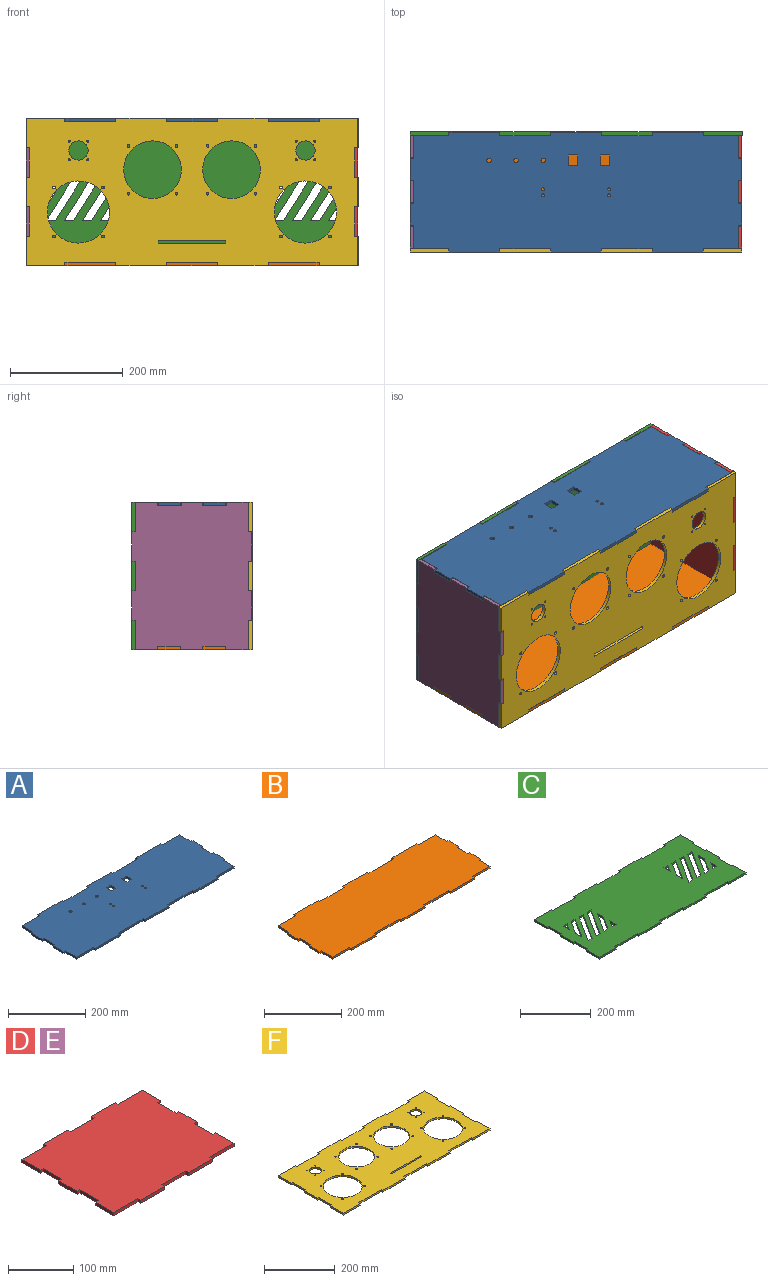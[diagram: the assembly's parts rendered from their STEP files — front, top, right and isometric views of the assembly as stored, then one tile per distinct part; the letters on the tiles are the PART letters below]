
ASSEMBLY  parts=6 mates=5
PART A: 61 faces, bbox 588x212x6 mm
  f0: plane 40x6mm, normal (-1,0,0), area 240mm2, adj f1,f58,f59,f60
  f1: plane 63x6mm, normal (0,-1,0), area 378mm2, adj f0,f2,f59,f60
  f2: plane 6x6mm, normal (-1,0,0), area 36mm2, adj f1,f3,f59,f60
  f3: plane 90x6mm, normal (0,-1,0), area 540mm2, adj f2,f4,f59,f60
  f4: plane 6x6mm, normal (1,0,0), area 36mm2, adj f3,f5,f59,f60
  f5: plane 90x6mm, normal (0,-1,0), area 540mm2, adj f4,f6,f59,f60
  f6: plane 6x6mm, normal (-1,0,0), area 36mm2, adj f5,f7,f59,f60
  f7: plane 90x6mm, normal (0,-1,0), area 540mm2, adj f6,f8,f59,f60
  f8: plane 6x6mm, normal (1,0,0), area 36mm2, adj f7,f9,f59,f60
  f9: plane 90x6mm, normal (0,-1,0), area 540mm2, adj f8,f10,f59,f60
  f10: plane 6x6mm, normal (-1,0,0), area 36mm2, adj f9,f11,f59,f60
  f11: plane 90x6mm, normal (0,-1,0), area 540mm2, adj f10,f12,f59,f60
  f12: plane 6x6mm, normal (1,0,0), area 36mm2, adj f11,f13,f59,f60
  f13: plane 63x6mm, normal (0,-1,0), area 378mm2, adj f12,f14,f59,f60
  f14: plane 40x6mm, normal (1,0,0), area 240mm2, adj f13,f15,f59,f60
  f15: plane 6x6mm, normal (0,-1,0), area 36mm2, adj f14,f16,f59,f60
  f16: plane 40x6mm, normal (1,0,0), area 240mm2, adj f15,f17,f59,f60
  f17: plane 6x6mm, normal (0,1,0), area 36mm2, adj f16,f18,f59,f60
  f18: plane 40x6mm, normal (1,0,0), area 240mm2, adj f17,f19,f59,f60
  f19: plane 6x6mm, normal (0,-1,0), area 36mm2, adj f18,f20,f59,f60
  f20: plane 40x6mm, normal (1,0,0), area 240mm2, adj f19,f21,f59,f60
  f21: plane 6x6mm, normal (0,1,0), area 36mm2, adj f20,f22,f59,f60
  f22: plane 40x6mm, normal (1,0,0), area 240mm2, adj f21,f23,f59,f60
  f23: plane 63x6mm, normal (0,1,0), area 378mm2, adj f22,f24,f59,f60
  f24: plane 6x6mm, normal (1,0,0), area 36mm2, adj f23,f25,f59,f60
  f25: plane 90x6mm, normal (0,1,0), area 540mm2, adj f24,f26,f59,f60
  f26: plane 6x6mm, normal (-1,0,0), area 36mm2, adj f25,f27,f59,f60
  f27: plane 90x6mm, normal (0,1,0), area 540mm2, adj f26,f28,f59,f60
  f28: plane 6x6mm, normal (1,0,0), area 36mm2, adj f27,f29,f59,f60
  f29: plane 90x6mm, normal (0,1,0), area 540mm2, adj f28,f30,f59,f60
  f30: plane 6x6mm, normal (-1,0,0), area 36mm2, adj f29,f31,f59,f60
  f31: plane 90x6mm, normal (0,1,0), area 540mm2, adj f30,f32,f59,f60
  f32: plane 6x6mm, normal (1,0,0), area 36mm2, adj f31,f33,f59,f60
  f33: plane 90x6mm, normal (0,1,0), area 540mm2, adj f32,f34,f59,f60
  f34: plane 6x6mm, normal (-1,0,0), area 36mm2, adj f33,f35,f59,f60
  f35: plane 63x6mm, normal (0,1,0), area 378mm2, adj f34,f36,f59,f60
  f36: plane 40x6mm, normal (-1,0,0), area 240mm2, adj f35,f37,f59,f60
  f37: plane 6x6mm, normal (0,1,0), area 36mm2, adj f36,f38,f59,f60
  f38: plane 40x6mm, normal (-1,0,0), area 240mm2, adj f37,f39,f59,f60
  f39: plane 6x6mm, normal (0,-1,0), area 36mm2, adj f38,f40,f59,f60
  f40: plane 40x6mm, normal (-1,0,0), area 240mm2, adj f39,f41,f59,f60
  f41: plane 6x6mm, normal (0,1,0), area 36mm2, adj f40,f42,f59,f60
  f42: plane 40x6mm, normal (-1,0,0), area 240mm2, adj f41,f58,f59,f60
  f43: plane 19x6mm, normal (1,0,0), area 114mm2, adj f44,f56,f59,f60
  f44: plane 17x6mm, normal (0,-1,0), area 102mm2, adj f43,f45,f59,f60
  f45: plane 19x6mm, normal (-1,0,0), area 114mm2, adj f44,f56,f59,f60
  f46: plane 19x6mm, normal (1,0,0), area 114mm2, adj f47,f57,f59,f60
  f47: plane 17x6mm, normal (0,-1,0), area 102mm2, adj f46,f48,f59,f60
  f48: plane 19x6mm, normal (-1,0,0), area 114mm2, adj f47,f57,f59,f60
  f49: cylinder r=4mm len=8mm, axis (0,0,-1), area 150.8mm2, adj f59,f60
  f50: cylinder r=4mm len=8mm, axis (0,0,-1), area 150.8mm2, adj f59,f60
  f51: cylinder r=4mm len=8mm, axis (0,0,-1), area 150.8mm2, adj f59,f60
  f52: cylinder r=2.5mm len=6mm, axis (0,0,-1), area 94.2mm2, adj f59,f60
  f53: cylinder r=2.5mm len=6mm, axis (0,0,-1), area 94.2mm2, adj f59,f60
  f54: cylinder r=2.5mm len=6mm, axis (0,0,-1), area 94.2mm2, adj f59,f60
  f55: cylinder r=2.5mm len=6mm, axis (0,0,-1), area 94.2mm2, adj f59,f60
  f56: plane 17x6mm, normal (0,1,0), area 102mm2, adj f43,f45,f59,f60
  f57: plane 17x6mm, normal (0,1,0), area 102mm2, adj f46,f48,f59,f60
  f58: plane 6x6mm, normal (0,-1,0), area 36mm2, adj f0,f42,f59,f60
  f59: plane 588x212mm, normal (0,0,1), area 118524.7mm2, adj f0,f1,f2,f3,f4,f5,f6,f7
  f60: plane 588x212mm, normal (0,0,-1), area 118524.7mm2, adj f0,f1,f2,f3,f4,f5,f6,f7
PART B: 46 faces, bbox 588x213.1x6 mm
  f0: plane 40x6mm, normal (-1,0,0), area 240mm2, adj f1,f43,f44,f45
  f1: plane 6x6mm, normal (0,-1,0), area 36mm2, adj f0,f2,f44,f45
  f2: plane 40x6mm, normal (-1,0,0), area 240mm2, adj f1,f3,f44,f45
  f3: plane 6x6mm, normal (0,1,0), area 36mm2, adj f2,f4,f44,f45
  f4: plane 40x6mm, normal (-1,0,0), area 240mm2, adj f3,f5,f44,f45
  f5: plane 6x6mm, normal (0,-1,0), area 36mm2, adj f4,f6,f44,f45
  f6: plane 40x6mm, normal (-1,0,0), area 240mm2, adj f5,f7,f44,f45
  f7: plane 63x6mm, normal (0,-1,0), area 378mm2, adj f6,f8,f44,f45
  f8: plane 6.78x6mm, normal (-1,0,0), area 40.7mm2, adj f7,f9,f44,f45
  f9: plane 90x6mm, normal (0,-1,0), area 540mm2, adj f8,f10,f44,f45
  f10: plane 6x6mm, normal (1,0,0), area 36mm2, adj f9,f11,f44,f45
  f11: plane 90x6mm, normal (0,-1,0), area 540mm2, adj f10,f12,f44,f45
  f12: plane 6x6mm, normal (-1,0,0), area 36mm2, adj f11,f13,f44,f45
  f13: plane 90x6mm, normal (0,-1,0), area 540mm2, adj f12,f14,f44,f45
  f14: plane 6x6mm, normal (1,0,0), area 36mm2, adj f13,f15,f44,f45
  f15: plane 90x6mm, normal (0,-1,0), area 540mm2, adj f14,f16,f44,f45
  f16: plane 6.4x6mm, normal (-1,0,0), area 38.4mm2, adj f15,f17,f44,f45
  f17: plane 90x6mm, normal (0,-1,0), area 540mm2, adj f16,f18,f44,f45
  f18: plane 7.14x6mm, normal (1,0,0), area 42.8mm2, adj f17,f19,f44,f45
  f19: plane 63x6mm, normal (0,-1,0), area 378mm2, adj f18,f20,f44,f45
  f20: plane 40x6mm, normal (1,0,0), area 240mm2, adj f19,f21,f44,f45
  f21: plane 6x6mm, normal (0,-1,0), area 36mm2, adj f20,f22,f44,f45
  f22: plane 40x6mm, normal (1,0,0), area 240mm2, adj f21,f23,f44,f45
  f23: plane 6x6mm, normal (0,1,0), area 36mm2, adj f22,f24,f44,f45
  f24: plane 40x6mm, normal (1,0,0), area 240mm2, adj f23,f25,f44,f45
  f25: plane 6x6mm, normal (0,-1,0), area 36mm2, adj f24,f26,f44,f45
  f26: plane 40x6mm, normal (1,0,0), area 240mm2, adj f25,f27,f44,f45
  f27: plane 6x6mm, normal (0,1,0), area 36mm2, adj f26,f28,f44,f45
  f28: plane 40x6mm, normal (1,0,0), area 240mm2, adj f27,f29,f44,f45
  f29: plane 63x6mm, normal (0,1,0), area 378mm2, adj f28,f30,f44,f45
  f30: plane 6x6mm, normal (1,0,0), area 36mm2, adj f29,f31,f44,f45
  f31: plane 90x6mm, normal (0,1,0), area 540mm2, adj f30,f32,f44,f45
  f32: plane 6x6mm, normal (-1,0,0), area 36mm2, adj f31,f33,f44,f45
  f33: plane 90x6mm, normal (0,1,0), area 540mm2, adj f32,f34,f44,f45
  f34: plane 6x6mm, normal (1,0,0), area 36mm2, adj f33,f35,f44,f45
  f35: plane 90x6mm, normal (0,1,0), area 540mm2, adj f34,f36,f44,f45
  f36: plane 6x6mm, normal (-1,0,0), area 36mm2, adj f35,f37,f44,f45
  f37: plane 90x6mm, normal (0,1,0), area 540mm2, adj f36,f38,f44,f45
  f38: plane 6x6mm, normal (1,0,0), area 36mm2, adj f37,f39,f44,f45
  f39: plane 90x6mm, normal (0,1,0), area 540mm2, adj f38,f40,f44,f45
  f40: plane 6x6mm, normal (-1,0,0), area 36mm2, adj f39,f41,f44,f45
  f41: plane 63x6mm, normal (0,1,0), area 378mm2, adj f40,f42,f44,f45
  f42: plane 40x6mm, normal (-1,0,0), area 240mm2, adj f41,f43,f44,f45
  f43: plane 6x6mm, normal (0,1,0), area 36mm2, adj f0,f42,f44,f45
  f44: plane 588x213.14mm, normal (0,0,1), area 119768.4mm2, adj f0,f1,f2,f3,f4,f5,f6,f7
  f45: plane 588x213.14mm, normal (0,0,-1), area 119768.4mm2, adj f0,f1,f2,f3,f4,f5,f6,f7
PART C: 90 faces, bbox 588x261x6 mm
  f0: plane 25x6mm, normal (1,0,0), area 150mm2, adj f1,f87,f88,f89
  f1: plane 16x6mm, normal (0,-1,0), area 96mm2, adj f0,f87,f88,f89
  f2: plane 25x16mm, normal (0.84,-0.54,0), area 178.1mm2, adj f3,f75,f88,f89
  f3: plane 25x6mm, normal (-1,0,0), area 150mm2, adj f2,f75,f88,f89
  f4: plane 16x6mm, normal (0,1,0), area 96mm2, adj f5,f76,f88,f89
  f5: plane 25x16mm, normal (0.84,-0.54,0), area 178.1mm2, adj f4,f76,f88,f89
  f6: plane 75x48mm, normal (0.84,-0.54,0), area 534.3mm2, adj f7,f77,f88,f89
  f7: plane 25x6mm, normal (-1,0,0), area 150mm2, adj f6,f8,f88,f89
  f8: plane 50x32mm, normal (-0.84,0.54,0), area 356.2mm2, adj f7,f77,f88,f89
  f9: plane 100x64mm, normal (0.84,-0.54,0), area 712.4mm2, adj f10,f78,f88,f89
  f10: plane 16x6mm, normal (0,-1,0), area 96mm2, adj f9,f11,f88,f89
  f11: plane 100x64mm, normal (-0.84,0.54,0), area 712.4mm2, adj f10,f78,f88,f89
  f12: plane 100x64mm, normal (0.84,-0.54,0), area 712.4mm2, adj f13,f79,f88,f89
  f13: plane 16x6mm, normal (0,-1,0), area 96mm2, adj f12,f14,f88,f89
  f14: plane 100x64mm, normal (-0.84,0.54,0), area 712.4mm2, adj f13,f79,f88,f89
  f15: plane 50x32mm, normal (0.84,-0.54,0), area 356.2mm2, adj f16,f80,f88,f89
  f16: plane 16x6mm, normal (0,-1,0), area 96mm2, adj f15,f17,f88,f89
  f17: plane 75x48mm, normal (-0.84,0.54,0), area 534.3mm2, adj f16,f80,f88,f89
  f18: plane 16x6mm, normal (0,-1,0), area 96mm2, adj f19,f81,f88,f89
  f19: plane 25x16mm, normal (-0.84,0.54,0), area 178.1mm2, adj f18,f81,f88,f89
  f20: plane 75x48mm, normal (0.84,-0.54,0), area 534.3mm2, adj f21,f82,f88,f89
  f21: plane 25x6mm, normal (-1,0,0), area 150mm2, adj f20,f22,f88,f89
  f22: plane 50x32mm, normal (-0.84,0.54,0), area 356.2mm2, adj f21,f82,f88,f89
  f23: plane 100x64mm, normal (0.84,-0.54,0), area 712.4mm2, adj f24,f83,f88,f89
  f24: plane 16x6mm, normal (0,-1,0), area 96mm2, adj f23,f25,f88,f89
  f25: plane 100x64mm, normal (-0.84,0.54,0), area 712.4mm2, adj f24,f83,f88,f89
  f26: plane 100x64mm, normal (0.84,-0.54,0), area 712.4mm2, adj f27,f84,f88,f89
  f27: plane 16x6mm, normal (0,-1,0), area 96mm2, adj f26,f28,f88,f89
  f28: plane 100x64mm, normal (-0.84,0.54,0), area 712.4mm2, adj f27,f84,f88,f89
  f29: plane 50x32mm, normal (0.84,-0.54,0), area 356.2mm2, adj f30,f85,f88,f89
  f30: plane 16x6mm, normal (0,-1,0), area 96mm2, adj f29,f31,f88,f89
  f31: plane 75x48mm, normal (-0.84,0.54,0), area 534.3mm2, adj f30,f85,f88,f89
  f32: plane 52.2x6mm, normal (-1,0,0), area 313.2mm2, adj f33,f86,f88,f89
  f33: plane 6x6mm, normal (0,1,0), area 36mm2, adj f32,f34,f88,f89
  f34: plane 52.2x6mm, normal (-1,0,0), area 313.2mm2, adj f33,f35,f88,f89
  f35: plane 69x6mm, normal (0,-1,0), area 414mm2, adj f34,f36,f88,f89
  f36: plane 6x6mm, normal (1,0,0), area 36mm2, adj f35,f37,f88,f89
  f37: plane 90x6mm, normal (0,-1,0), area 540mm2, adj f36,f38,f88,f89
  f38: plane 6x6mm, normal (-1,0,0), area 36mm2, adj f37,f39,f88,f89
  f39: plane 90x6mm, normal (0,-1,0), area 540mm2, adj f38,f40,f88,f89
  f40: plane 6x6mm, normal (1,0,0), area 36mm2, adj f39,f41,f88,f89
  f41: plane 90x6mm, normal (0,-1,0), area 540mm2, adj f40,f42,f88,f89
  f42: plane 6x6mm, normal (-1,0,0), area 36mm2, adj f41,f43,f88,f89
  f43: plane 90x6mm, normal (0,-1,0), area 540mm2, adj f42,f44,f88,f89
  f44: plane 6x6mm, normal (1,0,0), area 36mm2, adj f43,f45,f88,f89
  f45: plane 90x6mm, normal (0,-1,0), area 540mm2, adj f44,f46,f88,f89
  f46: plane 6x6mm, normal (-1,0,0), area 36mm2, adj f45,f47,f88,f89
  f47: plane 69x6mm, normal (0,-1,0), area 414mm2, adj f46,f48,f88,f89
  f48: plane 52.2x6mm, normal (1,0,0), area 313.2mm2, adj f47,f49,f88,f89
  f49: plane 6x6mm, normal (0,1,0), area 36mm2, adj f48,f50,f88,f89
  f50: plane 52.2x6mm, normal (1,0,0), area 313.2mm2, adj f49,f51,f88,f89
  f51: plane 6x6mm, normal (0,-1,0), area 36mm2, adj f50,f52,f88,f89
  f52: plane 52.2x6mm, normal (1,0,0), area 313.2mm2, adj f51,f53,f88,f89
  f53: plane 6x6mm, normal (0,1,0), area 36mm2, adj f52,f54,f88,f89
  f54: plane 52.2x6mm, normal (1,0,0), area 313.2mm2, adj f53,f55,f88,f89
  f55: plane 6x6mm, normal (0,-1,0), area 36mm2, adj f54,f56,f88,f89
  f56: plane 52.2x6mm, normal (1,0,0), area 313.2mm2, adj f55,f57,f88,f89
  f57: plane 69x6mm, normal (0,1,0), area 414mm2, adj f56,f58,f88,f89
  f58: plane 6x6mm, normal (-1,0,0), area 36mm2, adj f57,f59,f88,f89
  f59: plane 90x6mm, normal (0,1,0), area 540mm2, adj f58,f60,f88,f89
  f60: plane 6x6mm, normal (1,0,0), area 36mm2, adj f59,f61,f88,f89
  f61: plane 90x6mm, normal (0,1,0), area 540mm2, adj f60,f62,f88,f89
  f62: plane 6x6mm, normal (-1,0,0), area 36mm2, adj f61,f63,f88,f89
  f63: plane 90x6mm, normal (0,1,0), area 540mm2, adj f62,f64,f88,f89
  f64: plane 6x6mm, normal (1,0,0), area 36mm2, adj f63,f65,f88,f89
  f65: plane 90x6mm, normal (0,1,0), area 540mm2, adj f64,f66,f88,f89
  f66: plane 6x6mm, normal (-1,0,0), area 36mm2, adj f65,f67,f88,f89
  f67: plane 90x6mm, normal (0,1,0), area 540mm2, adj f66,f68,f88,f89
  f68: plane 6x6mm, normal (1,0,0), area 36mm2, adj f67,f69,f88,f89
  f69: plane 69x6mm, normal (0,1,0), area 414mm2, adj f68,f70,f88,f89
  f70: plane 52.2x6mm, normal (-1,0,0), area 313.2mm2, adj f69,f71,f88,f89
  f71: plane 6x6mm, normal (0,-1,0), area 36mm2, adj f70,f72,f88,f89
  f72: plane 52.2x6mm, normal (-1,0,0), area 313.2mm2, adj f71,f73,f88,f89
  f73: plane 6x6mm, normal (0,1,0), area 36mm2, adj f72,f74,f88,f89
  f74: plane 52.2x6mm, normal (-1,0,0), area 313.2mm2, adj f73,f86,f88,f89
  f75: plane 16x6mm, normal (0,1,0), area 96mm2, adj f2,f3,f88,f89
  f76: plane 25x6mm, normal (-1,0,0), area 150mm2, adj f4,f5,f88,f89
  f77: plane 16x6mm, normal (0,1,0), area 96mm2, adj f6,f8,f88,f89
  f78: plane 16x6mm, normal (0,1,0), area 96mm2, adj f9,f11,f88,f89
  f79: plane 16x6mm, normal (0,1,0), area 96mm2, adj f12,f14,f88,f89
  f80: plane 25x6mm, normal (1,0,0), area 150mm2, adj f15,f17,f88,f89
  f81: plane 25x6mm, normal (1,0,0), area 150mm2, adj f18,f19,f88,f89
  f82: plane 16x6mm, normal (0,1,0), area 96mm2, adj f20,f22,f88,f89
  f83: plane 16x6mm, normal (0,1,0), area 96mm2, adj f23,f25,f88,f89
  f84: plane 16x6mm, normal (0,1,0), area 96mm2, adj f26,f28,f88,f89
  f85: plane 25x6mm, normal (1,0,0), area 150mm2, adj f29,f31,f88,f89
  f86: plane 6x6mm, normal (0,-1,0), area 36mm2, adj f32,f74,f88,f89
  f87: plane 25x16mm, normal (-0.84,0.54,0), area 178.1mm2, adj f0,f1,f88,f89
  f88: plane 588x261mm, normal (0,0,1), area 137775.2mm2, adj f0,f1,f2,f3,f4,f5,f6,f7
  f89: plane 588x261mm, normal (0,0,-1), area 137775.2mm2, adj f0,f1,f2,f3,f4,f5,f6,f7
PART D: 38 faces, bbox 261x212x6 mm
  f0: plane 6x6mm, normal (0,-1,0), area 36mm2, adj f1,f35,f36,f37
  f1: plane 40x6mm, normal (-1,0,0), area 240mm2, adj f0,f2,f36,f37
  f2: plane 6x6mm, normal (0,1,0), area 36mm2, adj f1,f3,f36,f37
  f3: plane 40x6mm, normal (-1,0,0), area 240mm2, adj f2,f4,f36,f37
  f4: plane 52.2x6mm, normal (0,-1,0), area 313.2mm2, adj f3,f5,f36,f37
  f5: plane 6x6mm, normal (-1,0,0), area 36mm2, adj f4,f6,f36,f37
  f6: plane 52.2x6mm, normal (0,-1,0), area 313.2mm2, adj f5,f7,f36,f37
  f7: plane 6x6mm, normal (1,0,0), area 36mm2, adj f6,f8,f36,f37
  f8: plane 52.2x6mm, normal (0,-1,0), area 313.2mm2, adj f7,f9,f36,f37
  f9: plane 6x6mm, normal (-1,0,0), area 36mm2, adj f8,f10,f36,f37
  f10: plane 52.2x6mm, normal (0,-1,0), area 313.2mm2, adj f9,f11,f36,f37
  f11: plane 6x6mm, normal (1,0,0), area 36mm2, adj f10,f12,f36,f37
  f12: plane 52.2x6mm, normal (0,-1,0), area 313.2mm2, adj f11,f13,f36,f37
  f13: plane 40x6mm, normal (1,0,0), area 240mm2, adj f12,f14,f36,f37
  f14: plane 6x6mm, normal (0,1,0), area 36mm2, adj f13,f15,f36,f37
  f15: plane 40x6mm, normal (1,0,0), area 240mm2, adj f14,f16,f36,f37
  f16: plane 6x6mm, normal (0,-1,0), area 36mm2, adj f15,f17,f36,f37
  f17: plane 40x6mm, normal (1,0,0), area 240mm2, adj f16,f18,f36,f37
  f18: plane 6x6mm, normal (0,1,0), area 36mm2, adj f17,f19,f36,f37
  f19: plane 40x6mm, normal (1,0,0), area 240mm2, adj f18,f20,f36,f37
  f20: plane 6x6mm, normal (0,-1,0), area 36mm2, adj f19,f21,f36,f37
  f21: plane 40x6mm, normal (1,0,0), area 240mm2, adj f20,f22,f36,f37
  f22: plane 52.2x6mm, normal (0,1,0), area 313.2mm2, adj f21,f23,f36,f37
  f23: plane 6x6mm, normal (1,0,0), area 36mm2, adj f22,f24,f36,f37
  f24: plane 52.2x6mm, normal (0,1,0), area 313.2mm2, adj f23,f25,f36,f37
  f25: plane 6x6mm, normal (-1,0,0), area 36mm2, adj f24,f26,f36,f37
  f26: plane 52.2x6mm, normal (0,1,0), area 313.2mm2, adj f25,f27,f36,f37
  f27: plane 6x6mm, normal (1,0,0), area 36mm2, adj f26,f28,f36,f37
  f28: plane 52.2x6mm, normal (0,1,0), area 313.2mm2, adj f27,f29,f36,f37
  f29: plane 6x6mm, normal (-1,0,0), area 36mm2, adj f28,f30,f36,f37
  f30: plane 52.2x6mm, normal (0,1,0), area 313.2mm2, adj f29,f31,f36,f37
  f31: plane 40x6mm, normal (-1,0,0), area 240mm2, adj f30,f32,f36,f37
  f32: plane 6x6mm, normal (0,-1,0), area 36mm2, adj f31,f33,f36,f37
  f33: plane 40x6mm, normal (-1,0,0), area 240mm2, adj f32,f34,f36,f37
  f34: plane 6x6mm, normal (0,1,0), area 36mm2, adj f33,f35,f36,f37
  f35: plane 40x6mm, normal (-1,0,0), area 240mm2, adj f0,f34,f36,f37
  f36: plane 261x212mm, normal (0,0,1), area 52492.8mm2, adj f0,f1,f2,f3,f4,f5,f6,f7
  f37: plane 261x212mm, normal (0,0,-1), area 52492.8mm2, adj f0,f1,f2,f3,f4,f5,f6,f7
PART E: same geometry as D
PART F: 80 faces, bbox 588x261x6 mm
  f0: plane 69x6mm, normal (0,1,0), area 414mm2, adj f1,f75,f78,f79
  f1: plane 52.2x6mm, normal (-1,0,0), area 313.2mm2, adj f0,f2,f78,f79
  f2: plane 6x6mm, normal (0,-1,0), area 36mm2, adj f1,f3,f78,f79
  f3: plane 52.2x6mm, normal (-1,0,0), area 313.2mm2, adj f2,f4,f78,f79
  f4: plane 6x6mm, normal (0,1,0), area 36mm2, adj f3,f5,f78,f79
  f5: plane 52.2x6mm, normal (-1,0,0), area 313.2mm2, adj f4,f6,f78,f79
  f6: plane 6x6mm, normal (0,-1,0), area 36mm2, adj f5,f7,f78,f79
  f7: plane 52.2x6mm, normal (-1,0,0), area 313.2mm2, adj f6,f8,f78,f79
  f8: plane 6x6mm, normal (0,1,0), area 36mm2, adj f7,f9,f78,f79
  f9: plane 52.2x6mm, normal (-1,0,0), area 313.2mm2, adj f8,f10,f78,f79
  f10: plane 69x6mm, normal (0,-1,0), area 414mm2, adj f9,f11,f78,f79
  f11: plane 6x6mm, normal (1,0,0), area 36mm2, adj f10,f12,f78,f79
  f12: plane 90x6mm, normal (0,-1,0), area 540mm2, adj f11,f13,f78,f79
  f13: plane 6x6mm, normal (-1,0,0), area 36mm2, adj f12,f14,f78,f79
  f14: plane 90x6mm, normal (0,-1,0), area 540mm2, adj f13,f15,f78,f79
  f15: plane 6x6mm, normal (1,0,0), area 36mm2, adj f14,f16,f78,f79
  f16: plane 90x6mm, normal (0,-1,0), area 540mm2, adj f15,f17,f78,f79
  f17: plane 6x6mm, normal (-1,0,0), area 36mm2, adj f16,f18,f78,f79
  f18: plane 90x6mm, normal (0,-1,0), area 540mm2, adj f17,f19,f78,f79
  f19: plane 6x6mm, normal (1,0,0), area 36mm2, adj f18,f20,f78,f79
  f20: plane 90x6mm, normal (0,-1,0), area 540mm2, adj f19,f21,f78,f79
  f21: plane 6x6mm, normal (-1,0,0), area 36mm2, adj f20,f22,f78,f79
  f22: plane 69x6mm, normal (0,-1,0), area 414mm2, adj f21,f23,f78,f79
  f23: plane 52.2x6mm, normal (1,0,0), area 313.2mm2, adj f22,f24,f78,f79
  f24: plane 6x6mm, normal (0,1,0), area 36mm2, adj f23,f25,f78,f79
  f25: plane 52.2x6mm, normal (1,0,0), area 313.2mm2, adj f24,f26,f78,f79
  f26: plane 6x6mm, normal (0,-1,0), area 36mm2, adj f25,f27,f78,f79
  f27: plane 52.2x6mm, normal (1,0,0), area 313.2mm2, adj f26,f28,f78,f79
  f28: plane 6x6mm, normal (0,1,0), area 36mm2, adj f27,f29,f78,f79
  f29: plane 52.2x6mm, normal (1,0,0), area 313.2mm2, adj f28,f30,f78,f79
  f30: plane 6x6mm, normal (0,-1,0), area 36mm2, adj f29,f31,f78,f79
  f31: plane 52.2x6mm, normal (1,0,0), area 313.2mm2, adj f30,f32,f78,f79
  f32: plane 69x6mm, normal (0,1,0), area 414mm2, adj f31,f33,f78,f79
  f33: plane 6x6mm, normal (-1,0,0), area 36mm2, adj f32,f34,f78,f79
  f34: plane 90x6mm, normal (0,1,0), area 540mm2, adj f33,f35,f78,f79
  f35: plane 6x6mm, normal (1,0,0), area 36mm2, adj f34,f36,f78,f79
  f36: plane 90x6mm, normal (0,1,0), area 540mm2, adj f35,f37,f78,f79
  f37: plane 6x6mm, normal (-1,0,0), area 36mm2, adj f36,f38,f78,f79
  f38: plane 90x6mm, normal (0,1,0), area 540mm2, adj f37,f39,f78,f79
  f39: plane 6x6mm, normal (1,0,0), area 36mm2, adj f38,f40,f78,f79
  f40: plane 90x6mm, normal (0,1,0), area 540mm2, adj f39,f41,f78,f79
  f41: plane 6x6mm, normal (-1,0,0), area 36mm2, adj f40,f42,f78,f79
  f42: plane 90x6mm, normal (0,1,0), area 540mm2, adj f41,f75,f78,f79
  f43: plane 6x5mm, normal (1,0,0), area 30mm2, adj f44,f76,f78,f79
  f44: plane 120x6mm, normal (0,-1,0), area 720mm2, adj f43,f45,f78,f79
  f45: plane 6x5mm, normal (-1,0,0), area 30mm2, adj f44,f76,f78,f79
  f46: cylinder r=55mm len=110mm, axis (0,0,-1), area 2073.5mm2, adj f78,f79
  f47: cylinder r=17mm len=34mm, axis (0,0,-1), area 640.9mm2, adj f78,f79
  f48: cylinder r=17mm len=34mm, axis (0,0,-1), area 640.9mm2, adj f78,f79
  f49: cylinder r=51mm len=102mm, axis (0,0,-1), area 1922.7mm2, adj f78,f79
  f50: cylinder r=51mm len=102mm, axis (0,0,-1), area 1922.7mm2, adj f78,f79
  f51: cylinder r=2.5mm len=6mm, axis (0,0,-1), area 94.2mm2, adj f78,f79
  f52: cylinder r=2.5mm len=6mm, axis (0,0,-1), area 94.2mm2, adj f78,f79
  f53: cylinder r=2.5mm len=6mm, axis (0,0,-1), area 94.2mm2, adj f78,f79
  f54: cylinder r=2.5mm len=6mm, axis (0,0,-1), area 94.2mm2, adj f78,f79
  f55: cylinder r=2.5mm len=6mm, axis (0,0,-1), area 94.2mm2, adj f78,f79
  f56: cylinder r=2.5mm len=6mm, axis (0,0,-1), area 94.2mm2, adj f78,f79
  f57: cylinder r=2.5mm len=6mm, axis (0,0,-1), area 94.2mm2, adj f78,f79
  f58: cylinder r=2.5mm len=6mm, axis (0,0,-1), area 94.2mm2, adj f78,f79
  f59: cylinder r=1.5mm len=6mm, axis (0,0,-1), area 56.5mm2, adj f78,f79
  f60: cylinder r=1.5mm len=6mm, axis (0,0,-1), area 56.5mm2, adj f78,f79
  f61: cylinder r=1.5mm len=6mm, axis (0,0,-1), area 56.5mm2, adj f78,f79
  f62: cylinder r=1.5mm len=6mm, axis (0,0,-1), area 56.5mm2, adj f78,f79
  f63: cylinder r=1.5mm len=6mm, axis (0,0,-1), area 56.5mm2, adj f78,f79
  f64: cylinder r=1.5mm len=6mm, axis (0,0,-1), area 56.5mm2, adj f78,f79
  f65: cylinder r=2.5mm len=6mm, axis (0,0,-1), area 94.2mm2, adj f78,f79
  f66: cylinder r=2.5mm len=6mm, axis (0,0,-1), area 94.2mm2, adj f78,f79
  f67: cylinder r=2.5mm len=6mm, axis (0,0,-1), area 94.2mm2, adj f78,f79
  f68: cylinder r=2.5mm len=6mm, axis (0,0,-1), area 94.2mm2, adj f78,f79
  f69: cylinder r=2.5mm len=6mm, axis (0,0,-1), area 94.2mm2, adj f78,f79
  f70: cylinder r=2.5mm len=6mm, axis (0,0,-1), area 94.2mm2, adj f78,f79
  f71: cylinder r=2.5mm len=6mm, axis (0,0,-1), area 94.2mm2, adj f78,f79
  f72: cylinder r=2.5mm len=6mm, axis (0,0,-1), area 94.2mm2, adj f78,f79
  f73: cylinder r=1.5mm len=6mm, axis (0,0,-1), area 56.5mm2, adj f78,f79
  f74: cylinder r=1.5mm len=6mm, axis (0,0,-1), area 56.5mm2, adj f78,f79
  f75: plane 6x6mm, normal (1,0,0), area 36mm2, adj f0,f42,f78,f79
  f76: plane 120x6mm, normal (0,1,0), area 720mm2, adj f43,f45,f78,f79
  f77: cylinder r=55mm len=110mm, axis (0,0,-1), area 2073.5mm2, adj f78,f79
  f78: plane 588x261mm, normal (0,0,1), area 110839.5mm2, adj f0,f1,f2,f3,f4,f5,f6,f7
  f79: plane 588x261mm, normal (0,0,-1), area 110839.5mm2, adj f0,f1,f2,f3,f4,f5,f6,f7
PLACE A t=(69.62,123.78,249)mm
PLACE B t=(69.62,-183.62,-6)mm fixed
PLACE C rot(axis=(1,0,0),90deg) t=(69.62,106.01,919.94)mm
PLACE D rot(axis=(0,-1,0),90deg) t=(293.62,124.92,-285.08)mm
PLACE E rot(axis=(0,-1,0),90deg) t=(-288.38,124.92,-285.08)mm
PLACE F rot(axis=(1,0,0),90deg) t=(69.62,-101.13,562.29)mm
MATE fastened B.f44 <-> C.f45  axis (0,0,1) through (224.62,106.01,0)mm
MATE fastened B.f44 <-> F.f20  axis (0,0,1) through (224.62,-107.13,0)mm
MATE fastened A.f13 <-> F.f79  axis (0,-1,0) through (224.62,-101.13,255)mm
MATE fastened B.f44 <-> E.f1  axis (0,0,1) through (-294.38,-59.99,0)mm
MATE fastened B.f44 <-> D.f1  axis (0,0,1) through (293.62,-59.99,0)mm
